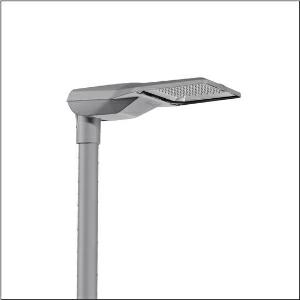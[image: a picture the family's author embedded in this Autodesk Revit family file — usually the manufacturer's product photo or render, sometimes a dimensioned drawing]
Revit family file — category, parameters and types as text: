
# Revit family: streetlight_sl_21_midi___pc-l_5xe7f43a08mb_85ee
name_source: partatom
category: Lighting Fixtures
units: mm (PartAtom-declared; Revit-internal decimal feet)

## family parameters
Cut with Voids When Loaded = No
Host = Face
Light Source = No
Part Type = Normal
Room Calculation Point = No
Round Connector Dimension = Use Diameter
Shared = No

## types (1)
- --- (1 x LED, 19200 lm, 147 W, 4000K)
    Apparent Load = 147 VA
    CIE Flux Codes = 38 78 98 100 100
    Color Rendering = 70
    Color Temperature = 4000K
    Default Elevation = 1800 mm
    Description = Streetlight SL 21 midi, mast luminaire, primary light control with lens, of PMMA, primary optical cover: cover, of toughened safety glass, transparent, light distribution: PC-L, light emission: direct distribution, primary light characteristic: asymmetric, left, installation type: post-top, side-entry, LED, 3G 1.5mm², High Power LED, rated luminous flux: 19.200lm, luminous efficacy: 131lm/W, light colour: 740, colour temperature: 4000K, control: overheat protection, constant luminous flux control, time-dependent luminous flux control, flexible luminous flux parameterisation, mains connection: 220..240V, AC, 50/60Hz, connection cable pre-assembled, cable length: 12,5m, wiring characteristics: H07RN-F, start of lifetime: 147W, end of service life: 155W, reduction: 64W, luminaire housing, of diecast aluminium, powder-coated, Siteco® metallic grey (DB 702S), corrosivity category C5 mid according to DIN EN ISO 12944, please order mast flange separately, inclination adjustable: 0°, 5°, 10°, 15°, sealing non-destructively replaceable, multi-level sealing system, length: 644mm, width: 335mm, height: 110mm, mast flange for spigot size: 42mm (side-entry): 5XC10008XM4, 60/48mm (side-entry/post-top): 5XC10108XM2, 76/60mm (side-entry/post-top): 5XC10108XM1, protection rating (complete): IP66, insulation class (complete): insulation class II (safety insulation), certification: CE, ENEC, ENEC+, VDE, impact resistance: IK09, permissible operating ambient temperature for outdoor applications: -40..+50°C, standard-compliant lighting for roads and squares, packaging unit: 1 piece

Light Distribution: PC-L
    Height = 111 mm
    Lamp = 1 x LED
    Lamp Light Flux = 19200 lm
    Lamp Power = 147 W
    Lamp count = 1
    Length = 644 mm
    Luminous efficacy = 131 lm/W
    Manufacturer = Siteco
    ModVariant = No
    Model = 5XE7F43A08MB
    Number of Poles = 1
    OnlyDefault = Yes
    Power Factor = 1
    Product Name = Streetlight SL 21 midi | PC-L
    Product group = mast luminaire | pylon top
    ProductGroupID = 6100
    Protection Class = Protection class II
    Protection Degree = IP 66
    RLX_Detail_Level = 1
    RLX_Emergency_Light_Flux = 0 lm
    RLX_Emergency_Type = 0
    RLX_Emergency_Type_DB = No
    RlxData = <blob elided: 92809 chars, md5=fbaf6a46>
    Socket = socket
    Standby Power = 0 W
    System Light Flux = 19200 lm
    System Power = 147 W
    Type Comments = factory setting: luminous flux: 100 % | Output Level: 100 % | 750 mA
    Type Image = l_1004298.jpg
    URL = http://relux.com
    VarID = @adj_022989
    Voltage = 0 V
    Weight = 0.00 kg
    Width = 336 mm

## geometry (parser evidence)
native form markers: Blend x4, Sweep x11
no freeform markers — native parametric forms only
